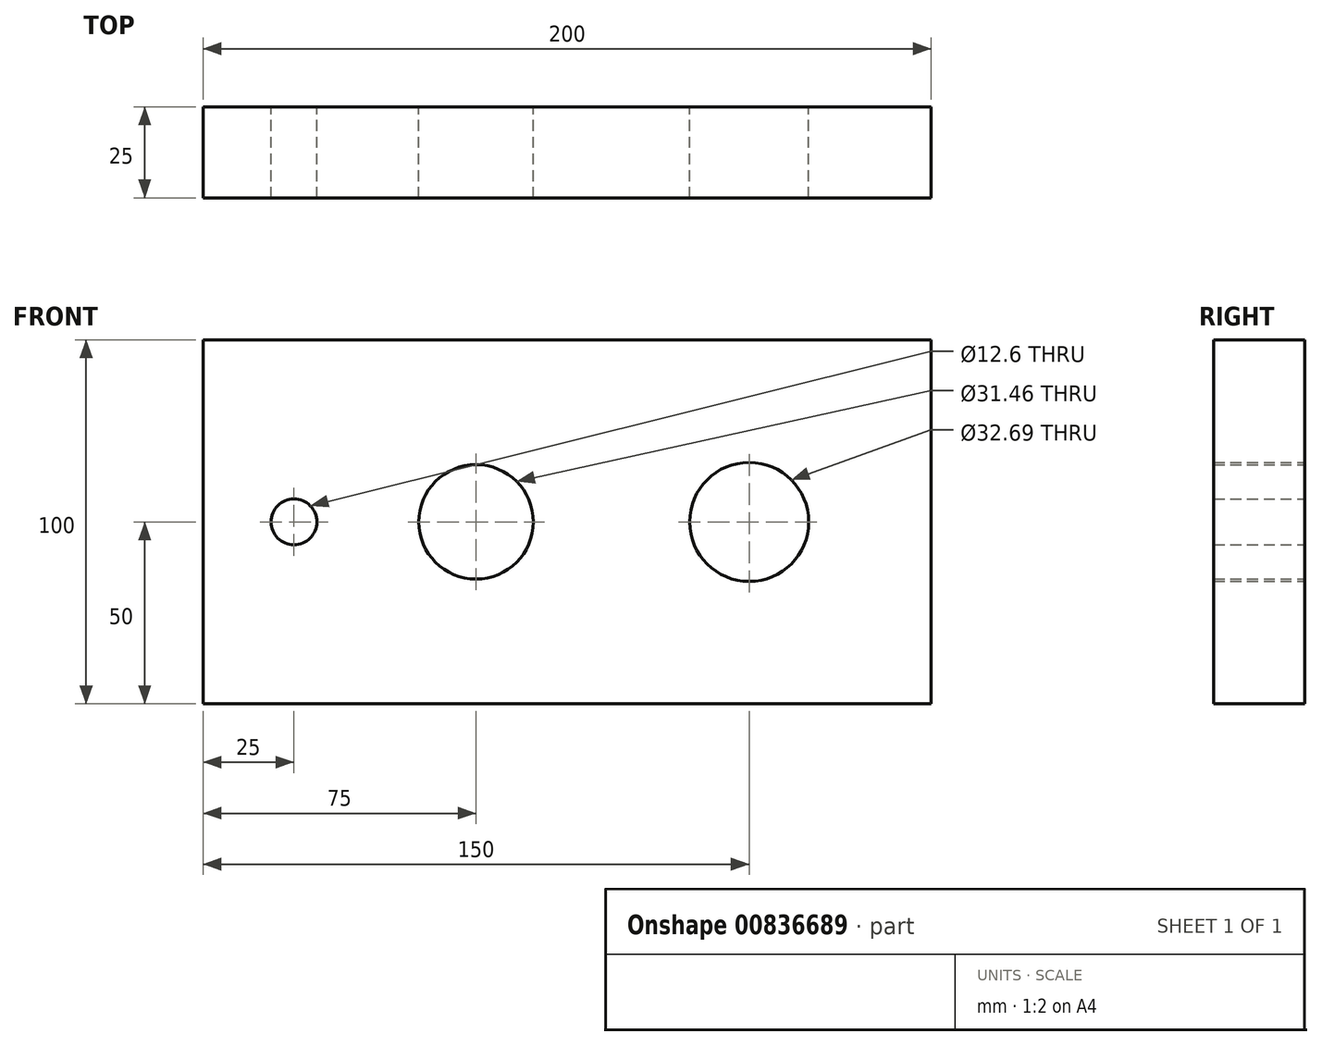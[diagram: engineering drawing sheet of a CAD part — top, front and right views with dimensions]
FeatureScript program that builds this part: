
annotation { "Feature Type Name" : "Feature", "Feature Type Description" : "" }
export const myFeature = defineFeature(function(context is Context, id is Id, definition is map)
    precondition{}
    {
        {
            var Q0;
            Q0=qCreatedBy(makeId("Front.planeOp"),FACE);
            var sketch = newSketch(context, id + "F0", { "sketchPlane" : qUnion([Q0])});
            skLineSegment(sketch, "E0.bottom", {"start": v(-100, 50) * mm, "end": v(100, 50) * mm});
            skLineSegment(sketch, "E0.top", {"start": v(-100, -50) * mm, "end": v(100, -50) * mm});
            skLineSegment(sketch, "E0.left", {"start": v(-100, 50) * mm, "end": v(-100, -50) * mm});
            skLineSegment(sketch, "E0.right", {"start": v(100, 50) * mm, "end": v(100, -50) * mm});
            skCircle(sketch, "E1", {"center": v(-75, 0) * mm, "radius": 6.3 * mm});
            skCircle(sketch, "E2", {"center": v(-25, 0) * mm, "radius": 15.73 * mm});
            skCircle(sketch, "E3", {"center": v(50, 0) * mm, "radius": 16.35 * mm});
            skSolve(sketch);
        }
        {
            var Q0;
            Q0=makeQuery(id+"F0.imprint","IMPRINT",FACE,{"disambiguationData":[TD([[makeQuery(id+"F0.imprint","IMPRINT",EDGE,{"derivedFrom":sQuery(id+"F0.wireOp",EDGE,"E0.bottom")}),-1.0]])]});
            extrude(context, id + "F1", {"entities" : qUnion([Q0]), "depth" : 25 * mm, "offsetDistance" : 25 * mm});
        }
    });
